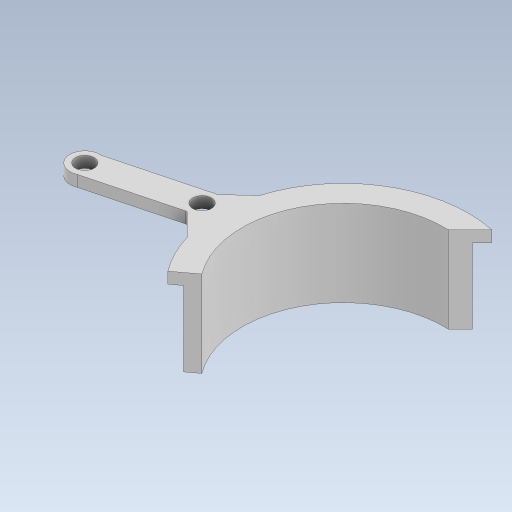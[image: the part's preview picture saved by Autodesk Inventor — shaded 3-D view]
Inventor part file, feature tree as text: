
AUTODESK INVENTOR PART (.ipt)
format: ipt  version: 2023.5 (Build 275446000, 446)  size: 317,952 bytes
history: native  units: mm
features: extrude x2, sketch x1
ambient origin geometry x8: Origin, YZ Plane, XZ Plane, XY Plane, X Axis, Y Axis, Z Axis, Center Point
bodies: Solid1 (feature_tree)
feature tree (3):
  sketch  "Sketch1"  dims[d8=3.0mm d9=0.0mm d10=3.0mm d11=0.0mm d14=135.0deg d15=20.0mm d16=0.0mm d17=25.0mm d18=67.0mm d19=61.0mm d20=58.0mm d21=8.0mm d22=5.0mm d23=8.0mm d24=5.0mm d25=19.0mm d27=54.0mm d28=20.0mm d29=45.0deg d26=0.5mm]
  extrude  "Extrusion1"  Depth=3.0mm TaperAngle=0.0deg
  extrude  "Extrusion2"  TaperAngle=135.0deg  [1 undecoded]
note: 1 required parameter value undecoded (feature->parameter linkage not recoverable at this tier; creation-order binding heuristic only, values carry confidence <= 0.55)
